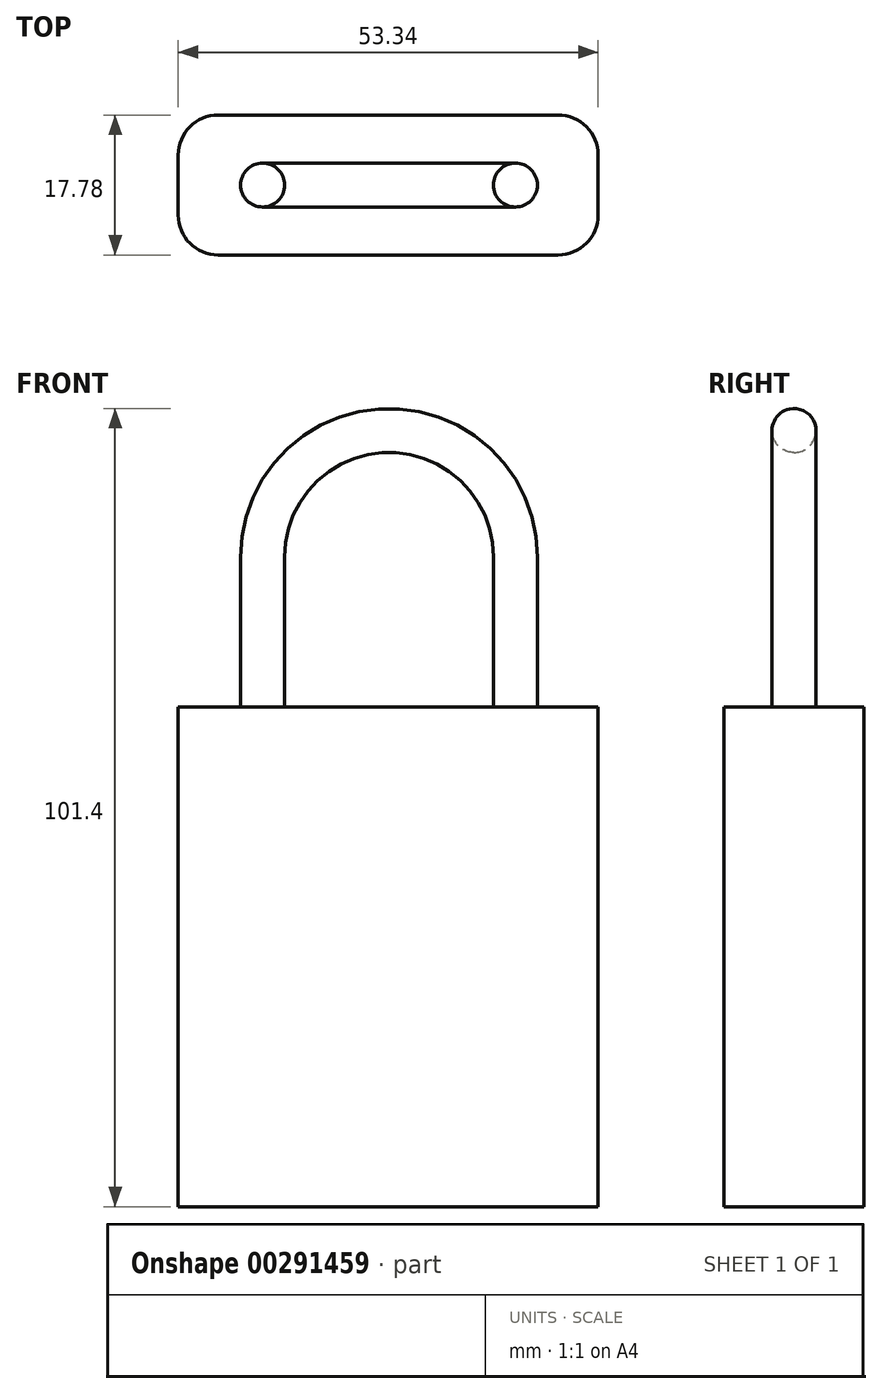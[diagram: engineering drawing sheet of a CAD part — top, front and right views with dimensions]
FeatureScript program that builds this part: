
annotation { "Feature Type Name" : "Feature", "Feature Type Description" : "" }
export const myFeature = defineFeature(function(context is Context, id is Id, definition is map)
    precondition{}
    {
        {
            var Q0;
            Q0=qCreatedBy(makeId("Front.planeOp"),FACE);
            var sketch = newSketch(context, id + "F0", { "sketchPlane" : qUnion([Q0])});
            skLineSegment(sketch, "E0", {"start": v(-16.05, 0) * mm, "end": v(-16.05, 19.05) * mm});
            skArc(sketch, "E1", {"start": v(-16.05, 19.05) * mm, "mid": v(0, 35.1) * mm, "end": v(16.05, 19.05) * mm});
            skLineSegment(sketch, "E2", {"start": v(16.05, 19.05) * mm, "end": v(16.05, 0) * mm});
            skSolve(sketch);
        }
        {
            var Q0;
            Q0=qCreatedBy(makeId("Top.planeOp"),FACE);
            var sketch = newSketch(context, id + "F1", { "sketchPlane" : qUnion([Q0])});
            skCircle(sketch, "E3", {"center": v(-16.05, 0) * mm, "radius": 2.8 * mm});
            skSolve(sketch);
        }
        {
            var Q0;
            Q0=makeQuery(id+"F1.imprint","IMPRINT",FACE,{"disambiguationData":[TD([[makeQuery(id+"F1.imprint","IMPRINT",EDGE,{"derivedFrom":sQuery(id+"F1.wireOp",EDGE,"E3")}),1.0]])]});
            var Q1;
            Q1 = qConstructionFilter(qBodyType(qCreatedBy(id + "F0" ,EDGE), BodyType.WIRE), ConstructionObject.NO);
            sweep(context, id + "F2", {"profiles" : qUnion([Q0]), "path" : qUnion([Q1])});
        }
        {
            var Q0;
            Q0=qCreatedBy(makeId("Front.planeOp"),FACE);
            var sketch = newSketch(context, id + "F3", { "sketchPlane" : qUnion([Q0])});
            skLineSegment(sketch, "E4.bottom", {"start": v(-26.78, 0) * mm, "end": v(26.56, 0) * mm});
            skLineSegment(sketch, "E4.top", {"start": v(-26.78, -63.5) * mm, "end": v(26.56, -63.5) * mm});
            skLineSegment(sketch, "E4.left", {"start": v(-26.78, 0) * mm, "end": v(-26.78, -63.5) * mm});
            skLineSegment(sketch, "E4.right", {"start": v(26.56, 0) * mm, "end": v(26.56, -63.5) * mm});
            skSolve(sketch);
        }
        {
            var Q0;
            Q0=makeQuery(id+"F3.imprint","IMPRINT",FACE,{"disambiguationData":[TD([[makeQuery(id+"F3.imprint","IMPRINT",EDGE,{"derivedFrom":sQuery(id+"F3.wireOp",EDGE,"E4.bottom")}),-1.0]])]});
            extrude(context, id + "F4", {"entities" : qUnion([Q0]), "operationType" : NewBodyOperationType.ADD, "endBound" : BoundingType.SYMMETRIC, "depth" : 17.78 * mm});
        }
        {
            var Q0;
            Q0=makeQuery(id+"F4.opExtrude","CAP_EDGE",EDGE,{"disambiguationData":[OSD([sQuery(id+"F3.wireOp",EDGE,"E4.left")])],"isStart":false});
            var Q1;
            Q1=makeQuery(id+"F4.opExtrude","CAP_EDGE",EDGE,{"disambiguationData":[OSD([sQuery(id+"F3.wireOp",EDGE,"E4.left")])],"isStart":true});
            var Q2;
            Q2=makeQuery(id+"F4.opExtrude","CAP_EDGE",EDGE,{"disambiguationData":[OSD([sQuery(id+"F3.wireOp",EDGE,"E4.right")])],"isStart":true});
            var Q3;
            Q3=makeQuery(id+"F4.opExtrude","CAP_EDGE",EDGE,{"disambiguationData":[OSD([sQuery(id+"F3.wireOp",EDGE,"E4.right")])],"isStart":false});
            fillet(context, id + "F5", {"entities" : qUnion([Q0, Q1, Q2, Q3]), "radius" : 5.08 * mm, "tangentPropagation" : true, "allowEdgeOverflow" : false});
        }
    });
